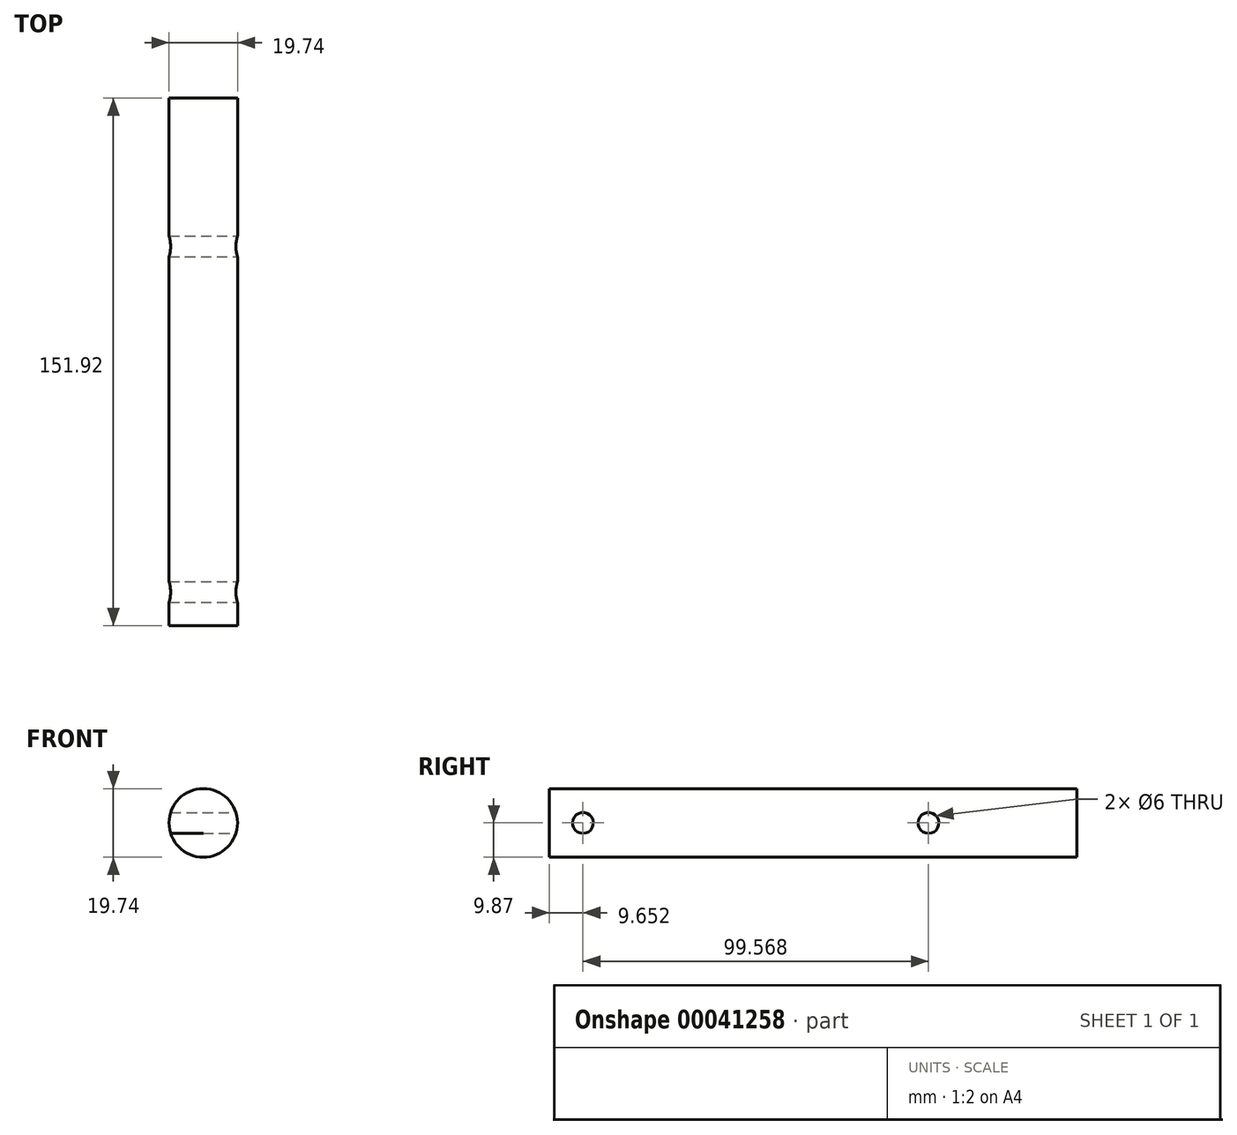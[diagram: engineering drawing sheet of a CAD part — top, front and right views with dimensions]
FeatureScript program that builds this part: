
annotation { "Feature Type Name" : "Feature", "Feature Type Description" : "" }
export const myFeature = defineFeature(function(context is Context, id is Id, definition is map)
    precondition{}
    {
        {
            var Q0;
            Q0=qCreatedBy(makeId("Front.planeOp"),FACE);
            var sketch = newSketch(context, id + "F0", { "sketchPlane" : qUnion([Q0])});
            skCircle(sketch, "E0", {"center": v(0, 0) * mm, "radius": 9.87 * mm});
            skSolve(sketch);
        }
        {
            var Q0;
            Q0 = qSketchRegion(id + "F0", true);
            extrude(context, id + "F1", {"entities" : qUnion([Q0]), "depth" : 151.92 * mm});
        }
        {
            var Q0;
            Q0=qCreatedBy(makeId("Right.planeOp"),FACE);
            cPlane(context, id + "F2", {"entities" : qUnion([Q0]), "cplaneType" : CPlaneType.OFFSET, "offset" : 15 * mm, "width" : 150 * mm, "height" : 150 * mm});
        }
        {
            var Q0;
            Q0=qCreatedBy(id+"F2.planeOp",FACE);
            var sketch = newSketch(context, id + "F3", { "sketchPlane" : qUnion([Q0])});
            skCircle(sketch, "E1", {"center": v(-142.27, 0) * mm, "radius": 3 * mm});
            skCircle(sketch, "E2", {"center": v(-42.7, 0) * mm, "radius": 3 * mm});
            skSolve(sketch);
        }
        {
            var Q0;
            Q0=makeQuery(id+"F3.imprint","IMPRINT",FACE,{"disambiguationData":[TD([[makeQuery(id+"F3.imprint","IMPRINT",EDGE,{"derivedFrom":sQuery(id+"F3.wireOp",EDGE,"E1")}),1.0]])]});
            var Q1;
            Q1=makeQuery(id+"F3.imprint","IMPRINT",FACE,{"disambiguationData":[TD([[makeQuery(id+"F3.imprint","IMPRINT",EDGE,{"derivedFrom":sQuery(id+"F3.wireOp",EDGE,"E2")}),1.0]])]});
            extrude(context, id + "F4", {"entities" : qUnion([Q0, Q1]), "operationType" : NewBodyOperationType.REMOVE, "endBound" : BoundingType.THROUGH_ALL, "oppositeDirection" : true, "depth" : 50 * mm});
        }
    });
